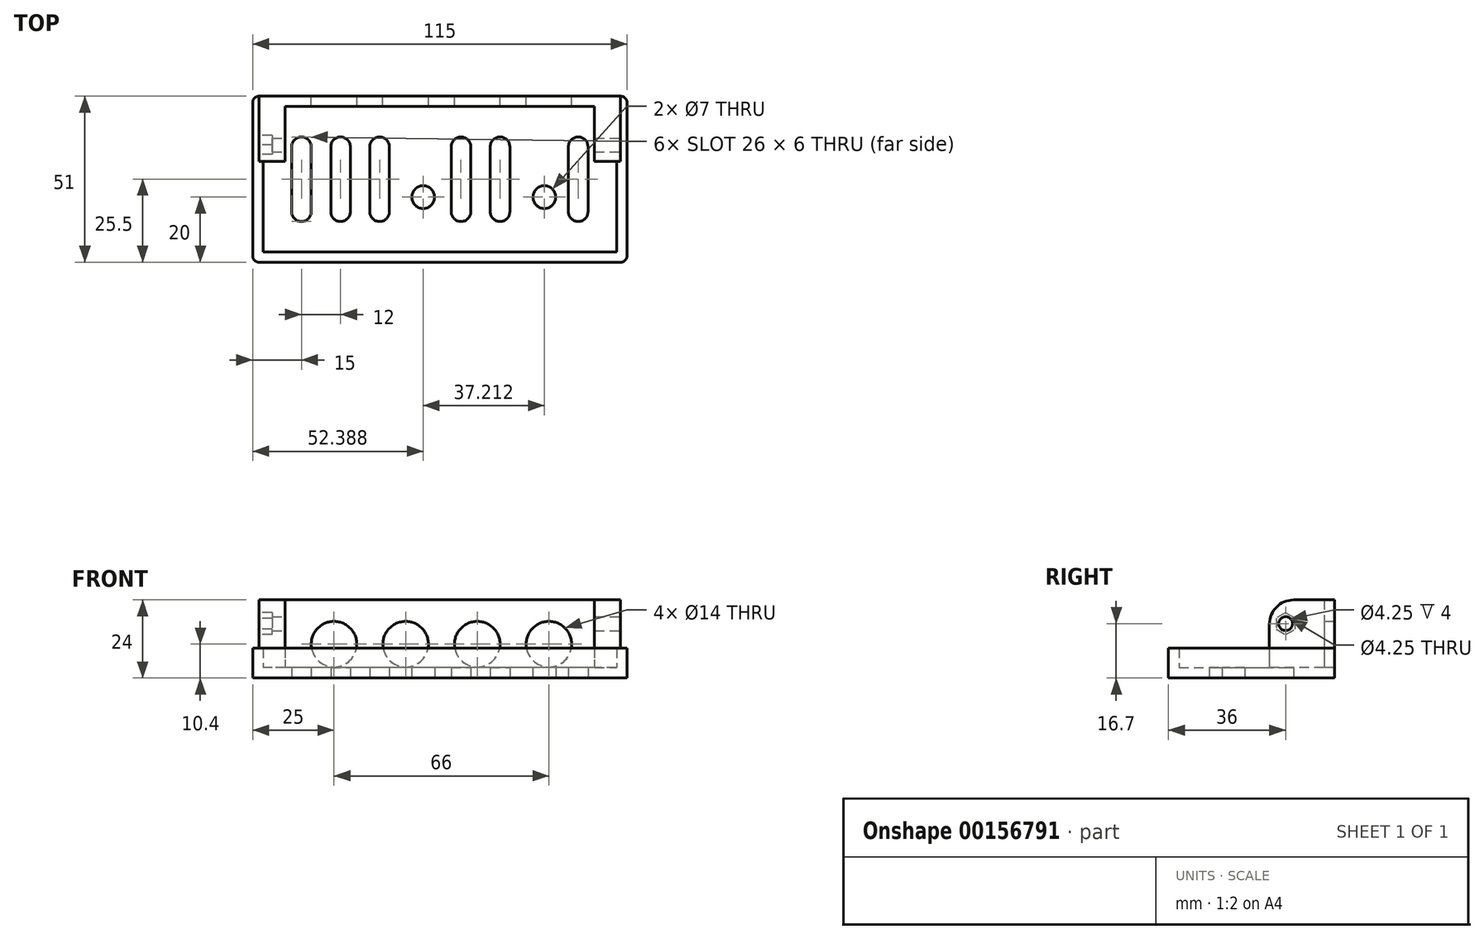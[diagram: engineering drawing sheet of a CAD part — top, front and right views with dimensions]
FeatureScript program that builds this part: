
annotation { "Feature Type Name" : "Feature", "Feature Type Description" : "" }
export const myFeature = defineFeature(function(context is Context, id is Id, definition is map)
    precondition{}
    {
        {
            var Q0;
            Q0=qCreatedBy(makeId("Top.planeOp"),FACE);
            var sketch = newSketch(context, id + "F0", { "sketchPlane" : qUnion([Q0])});
            skLineSegment(sketch, "E0.bottom", {"start": v(57.5, -25.5) * mm, "end": v(-57.5, -25.5) * mm});
            skLineSegment(sketch, "E0.top", {"start": v(57.5, 25.5) * mm, "end": v(-57.5, 25.5) * mm});
            skLineSegment(sketch, "E0.left", {"start": v(57.5, -25.5) * mm, "end": v(57.5, 25.5) * mm});
            skLineSegment(sketch, "E0.right", {"start": v(-57.5, -25.5) * mm, "end": v(-57.5, 25.5) * mm});
            skPoint(sketch, "E0.middle", {"position": v(0, 0) * mm});
            skLineSegment(sketch, "E1.bottom", {"start": v(-42.5, -13) * mm, "end": v(-42.5, -13) * mm});
            skLineSegment(sketch, "E1.top", {"start": v(-42.5, 13) * mm, "end": v(-42.5, 13) * mm});
            skLineSegment(sketch, "E1.left", {"start": v(-39.5, -10) * mm, "end": v(-39.5, 10) * mm});
            skLineSegment(sketch, "E1.right", {"start": v(-45.5, -10) * mm, "end": v(-45.5, 10) * mm});
            skPoint(sketch, "E1.middle", {"position": v(-42.5, 0) * mm});
            skLineSegment(sketch, "E2.bottom", {"start": v(-30.5, -13) * mm, "end": v(-30.5, -13) * mm});
            skLineSegment(sketch, "E2.top", {"start": v(-30.5, 13) * mm, "end": v(-30.5, 13) * mm});
            skLineSegment(sketch, "E2.left", {"start": v(-27.5, -10) * mm, "end": v(-27.5, 10) * mm});
            skLineSegment(sketch, "E2.right", {"start": v(-33.5, -10) * mm, "end": v(-33.5, 10) * mm});
            skPoint(sketch, "E2.middle", {"position": v(-30.5, 0) * mm});
            skLineSegment(sketch, "E3.bottom", {"start": v(-18.5, -13) * mm, "end": v(-18.5, -13) * mm});
            skLineSegment(sketch, "E3.top", {"start": v(-18.5, 13) * mm, "end": v(-18.5, 13) * mm});
            skLineSegment(sketch, "E3.left", {"start": v(-15.5, -10) * mm, "end": v(-15.5, 10) * mm});
            skLineSegment(sketch, "E3.right", {"start": v(-21.5, -10) * mm, "end": v(-21.5, 10) * mm});
            skPoint(sketch, "E3.middle", {"position": v(-18.5, 0) * mm});
            skLineSegment(sketch, "E4.bottom", {"start": v(6.5, -13) * mm, "end": v(6.5, -13) * mm});
            skLineSegment(sketch, "E4.top", {"start": v(6.5, 13) * mm, "end": v(6.5, 13) * mm});
            skLineSegment(sketch, "E4.left", {"start": v(9.5, -10) * mm, "end": v(9.5, 10) * mm});
            skLineSegment(sketch, "E4.right", {"start": v(3.5, -10) * mm, "end": v(3.5, 10) * mm});
            skPoint(sketch, "E4.middle", {"position": v(6.5, 0) * mm});
            skLineSegment(sketch, "E5.bottom", {"start": v(18.5, -13) * mm, "end": v(18.5, -13) * mm});
            skLineSegment(sketch, "E5.top", {"start": v(18.5, 13) * mm, "end": v(18.5, 13) * mm});
            skLineSegment(sketch, "E5.left", {"start": v(21.5, -10) * mm, "end": v(21.5, 10) * mm});
            skLineSegment(sketch, "E5.right", {"start": v(15.5, -10) * mm, "end": v(15.5, 10) * mm});
            skPoint(sketch, "E5.middle", {"position": v(18.5, 0) * mm});
            skLineSegment(sketch, "E6.bottom", {"start": v(42.5, -13) * mm, "end": v(42.5, -13) * mm});
            skLineSegment(sketch, "E6.top", {"start": v(42.5, 13) * mm, "end": v(42.5, 13) * mm});
            skLineSegment(sketch, "E6.left", {"start": v(45.5, -10) * mm, "end": v(45.5, 10) * mm});
            skLineSegment(sketch, "E6.right", {"start": v(39.5, -10) * mm, "end": v(39.5, 10) * mm});
            skPoint(sketch, "E6.middle", {"position": v(42.5, 0) * mm});
            skCircle(sketch, "E7", {"center": v(32.1, -5.5) * mm, "radius": 3.5 * mm});
            skCircle(sketch, "E8", {"center": v(-5.11, -5.5) * mm, "radius": 3.5 * mm});
            skPoint(sketch, "E9.visualSharp", {"position": v(-45.5, 13) * mm});
            skArc(sketch, "E9.filletArc", {"start": v(-42.5, 13) * mm, "mid": v(-44.62, 12.12) * mm, "end": v(-45.5, 10) * mm});
            skPoint(sketch, "E10.visualSharp", {"position": v(-39.5, 13) * mm});
            skArc(sketch, "E10.filletArc", {"start": v(-39.5, 10) * mm, "mid": v(-40.38, 12.12) * mm, "end": v(-42.5, 13) * mm});
            skPoint(sketch, "E11.visualSharp", {"position": v(-39.5, -13) * mm});
            skArc(sketch, "E11.filletArc", {"start": v(-42.5, -13) * mm, "mid": v(-40.38, -12.12) * mm, "end": v(-39.5, -10) * mm});
            skPoint(sketch, "E12.visualSharp", {"position": v(-45.5, -13) * mm});
            skArc(sketch, "E12.filletArc", {"start": v(-45.5, -10) * mm, "mid": v(-44.62, -12.12) * mm, "end": v(-42.5, -13) * mm});
            skPoint(sketch, "E13.visualSharp", {"position": v(-33.5, -13) * mm});
            skArc(sketch, "E13.filletArc", {"start": v(-33.5, -10) * mm, "mid": v(-32.62, -12.12) * mm, "end": v(-30.5, -13) * mm});
            skPoint(sketch, "E14.visualSharp", {"position": v(-27.5, -13) * mm});
            skArc(sketch, "E14.filletArc", {"start": v(-30.5, -13) * mm, "mid": v(-28.38, -12.12) * mm, "end": v(-27.5, -10) * mm});
            skPoint(sketch, "E15.visualSharp", {"position": v(-27.5, 13) * mm});
            skArc(sketch, "E15.filletArc", {"start": v(-27.5, 10) * mm, "mid": v(-28.38, 12.12) * mm, "end": v(-30.5, 13) * mm});
            skPoint(sketch, "E16.visualSharp", {"position": v(-33.5, 13) * mm});
            skArc(sketch, "E16.filletArc", {"start": v(-30.5, 13) * mm, "mid": v(-32.62, 12.12) * mm, "end": v(-33.5, 10) * mm});
            skPoint(sketch, "E17.visualSharp", {"position": v(-21.5, 13) * mm});
            skArc(sketch, "E17.filletArc", {"start": v(-18.5, 13) * mm, "mid": v(-20.62, 12.12) * mm, "end": v(-21.5, 10) * mm});
            skPoint(sketch, "E18.visualSharp", {"position": v(-15.5, 13) * mm});
            skArc(sketch, "E18.filletArc", {"start": v(-15.5, 10) * mm, "mid": v(-16.38, 12.12) * mm, "end": v(-18.5, 13) * mm});
            skPoint(sketch, "E19.visualSharp", {"position": v(-15.5, -13) * mm});
            skArc(sketch, "E19.filletArc", {"start": v(-18.5, -13) * mm, "mid": v(-16.38, -12.12) * mm, "end": v(-15.5, -10) * mm});
            skPoint(sketch, "E20.visualSharp", {"position": v(-21.5, -13) * mm});
            skArc(sketch, "E20.filletArc", {"start": v(-21.5, -10) * mm, "mid": v(-20.62, -12.12) * mm, "end": v(-18.5, -13) * mm});
            skPoint(sketch, "E21.visualSharp", {"position": v(3.5, -13) * mm});
            skArc(sketch, "E21.filletArc", {"start": v(3.5, -10) * mm, "mid": v(4.38, -12.12) * mm, "end": v(6.5, -13) * mm});
            skPoint(sketch, "E22.visualSharp", {"position": v(9.5, -13) * mm});
            skArc(sketch, "E22.filletArc", {"start": v(6.5, -13) * mm, "mid": v(8.62, -12.12) * mm, "end": v(9.5, -10) * mm});
            skPoint(sketch, "E23.visualSharp", {"position": v(9.5, 13) * mm});
            skArc(sketch, "E23.filletArc", {"start": v(9.5, 10) * mm, "mid": v(8.62, 12.12) * mm, "end": v(6.5, 13) * mm});
            skPoint(sketch, "E24.visualSharp", {"position": v(3.5, 13) * mm});
            skArc(sketch, "E24.filletArc", {"start": v(6.5, 13) * mm, "mid": v(4.38, 12.12) * mm, "end": v(3.5, 10) * mm});
            skPoint(sketch, "E25.visualSharp", {"position": v(15.5, -13) * mm});
            skArc(sketch, "E25.filletArc", {"start": v(15.5, -10) * mm, "mid": v(16.38, -12.12) * mm, "end": v(18.5, -13) * mm});
            skPoint(sketch, "E26.visualSharp", {"position": v(21.5, -13) * mm});
            skArc(sketch, "E26.filletArc", {"start": v(18.5, -13) * mm, "mid": v(20.62, -12.12) * mm, "end": v(21.5, -10) * mm});
            skPoint(sketch, "E27.visualSharp", {"position": v(21.5, 13) * mm});
            skArc(sketch, "E27.filletArc", {"start": v(21.5, 10) * mm, "mid": v(20.62, 12.12) * mm, "end": v(18.5, 13) * mm});
            skPoint(sketch, "E28.visualSharp", {"position": v(15.5, 13) * mm});
            skArc(sketch, "E28.filletArc", {"start": v(18.5, 13) * mm, "mid": v(16.38, 12.12) * mm, "end": v(15.5, 10) * mm});
            skPoint(sketch, "E29.visualSharp", {"position": v(39.5, -13) * mm});
            skArc(sketch, "E29.filletArc", {"start": v(39.5, -10) * mm, "mid": v(40.38, -12.12) * mm, "end": v(42.5, -13) * mm});
            skPoint(sketch, "E30.visualSharp", {"position": v(45.5, 13) * mm});
            skArc(sketch, "E30.filletArc", {"start": v(45.5, 10) * mm, "mid": v(44.62, 12.12) * mm, "end": v(42.5, 13) * mm});
            skPoint(sketch, "E31.visualSharp", {"position": v(39.5, 13) * mm});
            skArc(sketch, "E31.filletArc", {"start": v(42.5, 13) * mm, "mid": v(40.38, 12.12) * mm, "end": v(39.5, 10) * mm});
            skPoint(sketch, "E32.visualSharp", {"position": v(45.5, -13) * mm});
            skArc(sketch, "E32.filletArc", {"start": v(42.5, -13) * mm, "mid": v(44.62, -12.12) * mm, "end": v(45.5, -10) * mm});
            skSolve(sketch);
        }
        {
            var Q0;
            Q0 = qSketchRegion(id + "F0", true);
            extrude(context, id + "F1", {"entities" : qUnion([Q0]), "depth" : 3.2 * mm});
        }
        {
            var Q0;
            Q0=makeQuery(id+"F1.opExtrude","CAP_FACE",FACE,{"disambiguationData":[OSD([sQuery(id+"F0.wireOp",EDGE,"E0.bottom"),sQuery(id+"F0.wireOp",EDGE,"E0.top"),sQuery(id+"F0.wireOp",EDGE,"E0.left"),sQuery(id+"F0.wireOp",EDGE,"E0.right"),sQuery(id+"F0.wireOp",EDGE,"E1.bottom"),sQuery(id+"F0.wireOp",EDGE,"E1.top"),sQuery(id+"F0.wireOp",EDGE,"E1.left"),sQuery(id+"F0.wireOp",EDGE,"E1.right"),sQuery(id+"F0.wireOp",EDGE,"E2.bottom"),sQuery(id+"F0.wireOp",EDGE,"E2.top"),sQuery(id+"F0.wireOp",EDGE,"E2.left"),sQuery(id+"F0.wireOp",EDGE,"E2.right"),sQuery(id+"F0.wireOp",EDGE,"E3.bottom"),sQuery(id+"F0.wireOp",EDGE,"E3.top"),sQuery(id+"F0.wireOp",EDGE,"E3.left"),sQuery(id+"F0.wireOp",EDGE,"E3.right"),sQuery(id+"F0.wireOp",EDGE,"E4.bottom"),sQuery(id+"F0.wireOp",EDGE,"E4.top"),sQuery(id+"F0.wireOp",EDGE,"E4.left"),sQuery(id+"F0.wireOp",EDGE,"E4.right"),sQuery(id+"F0.wireOp",EDGE,"E5.bottom"),sQuery(id+"F0.wireOp",EDGE,"E5.top"),sQuery(id+"F0.wireOp",EDGE,"E5.left"),sQuery(id+"F0.wireOp",EDGE,"E5.right"),sQuery(id+"F0.wireOp",EDGE,"E6.bottom"),sQuery(id+"F0.wireOp",EDGE,"E6.top"),sQuery(id+"F0.wireOp",EDGE,"E6.left"),sQuery(id+"F0.wireOp",EDGE,"E6.right"),sQuery(id+"F0.wireOp",EDGE,"E7"),sQuery(id+"F0.wireOp",EDGE,"E8")])],"isStart":true});
            var sketch = newSketch(context, id + "F2", { "sketchPlane" : qUnion([Q0])});
            skLineSegment(sketch, "E33", {"start": v(-55.5, -5.5) * mm, "end": v(-55.5, -25.5) * mm});
            skLineSegment(sketch, "E34", {"start": v(-55.5, -25.5) * mm, "end": v(55.5, -25.5) * mm});
            skLineSegment(sketch, "E35", {"start": v(55.5, -25.5) * mm, "end": v(55.5, -5.5) * mm});
            skLineSegment(sketch, "E36", {"start": v(55.5, -5.5) * mm, "end": v(47.5, -5.5) * mm});
            skLineSegment(sketch, "E37", {"start": v(47.5, -5.5) * mm, "end": v(47.5, -22.3) * mm});
            skLineSegment(sketch, "E38", {"start": v(-55.5, -5.5) * mm, "end": v(-47.5, -5.5) * mm});
            skLineSegment(sketch, "E39", {"start": v(-47.5, -5.5) * mm, "end": v(-47.5, -22.3) * mm});
            skLineSegment(sketch, "E40", {"start": v(-47.5, -22.3) * mm, "end": v(47.5, -22.3) * mm});
            skSolve(sketch);
        }
        {
            var Q0;
            Q0 = qSketchRegion(id + "F2", true);
            extrude(context, id + "F3", {"entities" : qUnion([Q0]), "operationType" : NewBodyOperationType.ADD, "oppositeDirection" : true, "depth" : 24 * mm});
        }
        {
            var Q0;
            Q0=makeQuery(id+"F1.opExtrude","CAP_FACE",FACE,{"disambiguationData":[OSD([sQuery(id+"F0.wireOp",EDGE,"E0.bottom"),sQuery(id+"F0.wireOp",EDGE,"E0.top"),sQuery(id+"F0.wireOp",EDGE,"E0.left"),sQuery(id+"F0.wireOp",EDGE,"E0.right"),sQuery(id+"F0.wireOp",EDGE,"E1.left"),sQuery(id+"F0.wireOp",EDGE,"E1.right"),sQuery(id+"F0.wireOp",EDGE,"E2.left"),sQuery(id+"F0.wireOp",EDGE,"E2.right"),sQuery(id+"F0.wireOp",EDGE,"E3.left"),sQuery(id+"F0.wireOp",EDGE,"E3.right"),sQuery(id+"F0.wireOp",EDGE,"E4.left"),sQuery(id+"F0.wireOp",EDGE,"E4.right"),sQuery(id+"F0.wireOp",EDGE,"E5.left"),sQuery(id+"F0.wireOp",EDGE,"E5.right"),sQuery(id+"F0.wireOp",EDGE,"E6.left"),sQuery(id+"F0.wireOp",EDGE,"E6.right"),sQuery(id+"F0.wireOp",EDGE,"E7"),sQuery(id+"F0.wireOp",EDGE,"E8"),sQuery(id+"F0.wireOp",EDGE,"E9.filletArc"),sQuery(id+"F0.wireOp",EDGE,"E10.filletArc"),sQuery(id+"F0.wireOp",EDGE,"E11.filletArc"),sQuery(id+"F0.wireOp",EDGE,"E12.filletArc"),sQuery(id+"F0.wireOp",EDGE,"E13.filletArc"),sQuery(id+"F0.wireOp",EDGE,"E14.filletArc"),sQuery(id+"F0.wireOp",EDGE,"E15.filletArc"),sQuery(id+"F0.wireOp",EDGE,"E16.filletArc"),sQuery(id+"F0.wireOp",EDGE,"E17.filletArc"),sQuery(id+"F0.wireOp",EDGE,"E18.filletArc"),sQuery(id+"F0.wireOp",EDGE,"E19.filletArc"),sQuery(id+"F0.wireOp",EDGE,"E20.filletArc"),sQuery(id+"F0.wireOp",EDGE,"E21.filletArc"),sQuery(id+"F0.wireOp",EDGE,"E22.filletArc"),sQuery(id+"F0.wireOp",EDGE,"E23.filletArc"),sQuery(id+"F0.wireOp",EDGE,"E24.filletArc"),sQuery(id+"F0.wireOp",EDGE,"E25.filletArc"),sQuery(id+"F0.wireOp",EDGE,"E26.filletArc"),sQuery(id+"F0.wireOp",EDGE,"E27.filletArc"),sQuery(id+"F0.wireOp",EDGE,"E28.filletArc"),sQuery(id+"F0.wireOp",EDGE,"E29.filletArc"),sQuery(id+"F0.wireOp",EDGE,"E30.filletArc"),sQuery(id+"F0.wireOp",EDGE,"E31.filletArc"),sQuery(id+"F0.wireOp",EDGE,"E32.filletArc")])],"isStart":false});
            var sketch = newSketch(context, id + "F4", { "sketchPlane" : qUnion([Q0])});
            skLineSegment(sketch, "E41", {"start": v(-55.5, 25.5) * mm, "end": v(-57.5, 25.5) * mm});
            skLineSegment(sketch, "E42", {"start": v(-57.5, 25.5) * mm, "end": v(-57.5, -25.5) * mm});
            skLineSegment(sketch, "E43", {"start": v(-57.5, -25.5) * mm, "end": v(57.5, -25.5) * mm});
            skLineSegment(sketch, "E44", {"start": v(57.5, -25.5) * mm, "end": v(57.5, 25.5) * mm});
            skLineSegment(sketch, "E45", {"start": v(57.5, 25.5) * mm, "end": v(55.5, 25.5) * mm});
            skLineSegment(sketch, "E46", {"start": v(55.5, 25.5) * mm, "end": v(55.5, 5.5) * mm});
            skLineSegment(sketch, "E47", {"start": v(55.5, 5.5) * mm, "end": v(54.3, 5.5) * mm});
            skLineSegment(sketch, "E48", {"start": v(54.3, 5.5) * mm, "end": v(54.3, -22.3) * mm});
            skLineSegment(sketch, "E49", {"start": v(54.3, -22.3) * mm, "end": v(-54.3, -22.3) * mm});
            skLineSegment(sketch, "E50", {"start": v(-54.3, -22.3) * mm, "end": v(-54.3, 5.5) * mm});
            skLineSegment(sketch, "E51", {"start": v(-54.3, 5.5) * mm, "end": v(-55.5, 5.5) * mm});
            skLineSegment(sketch, "E52", {"start": v(-55.5, 5.5) * mm, "end": v(-55.5, 25.5) * mm});
            skLineSegment(sketch, "E53", {"start": v(54.3, 5.5) * mm, "end": v(55.5, 5.5) * mm});
            skSolve(sketch);
        }
        {
            var Q0;
            Q0 = qSketchRegion(id + "F4", true);
            extrude(context, id + "F5", {"entities" : qUnion([Q0]), "operationType" : NewBodyOperationType.ADD, "depth" : 6 * mm});
        }
        {
            var Q0;
            Q0=makeQuery(id+"F3.opExtrude","SWEPT_FACE",FACE,{"disambiguationData":[OSD([sQuery(id+"F2.wireOp",EDGE,"E35")])]});
            var sketch = newSketch(context, id + "F6", { "sketchPlane" : qUnion([Q0])});
            skCircle(sketch, "E54", {"center": v(10.5, 16.7) * mm, "radius": 2.12 * mm});
            skSolve(sketch);
        }
        {
            var Q0;
            Q0 = qSketchRegion(id + "F6", true);
            extrude(context, id + "F7", {"entities" : qUnion([Q0]), "operationType" : NewBodyOperationType.REMOVE, "endBound" : BoundingType.THROUGH_ALL, "oppositeDirection" : true, "depth" : 25 * mm});
        }
        {
            var Q0;
            Q0=makeQuery(id+"F3.opExtrude","CAP_EDGE",EDGE,{"disambiguationData":[OSD([sQuery(id+"F2.wireOp",EDGE,"E36")])],"isStart":false});
            var Q1;
            Q1=makeQuery(id+"F3.opExtrude","CAP_EDGE",EDGE,{"disambiguationData":[OSD([sQuery(id+"F2.wireOp",EDGE,"E38")])],"isStart":false});
            fillet(context, id + "F8", {"entities" : qUnion([Q0, Q1]), "radius" : 7.5 * mm, "tangentPropagation" : true, "allowEdgeOverflow" : false});
        }
        {
            var Q0;
            Q0=makeQuery(id+"F5.boolean.opBoolean","MERGE",EDGE,{"derivedFrom":[makeQuery(id+"F1.opExtrude","SWEPT_EDGE",EDGE,{"disambiguationData":[OSD([sQuery(id+"F0.wireOp",EDGE,"E0.bottom"),sQuery(id+"F0.wireOp",EDGE,"E0.right")])]}),makeQuery(id+"F5.opExtrude","SWEPT_EDGE",EDGE,{"disambiguationData":[OSD([sQuery(id+"F4.wireOp",EDGE,"E42"),sQuery(id+"F4.wireOp",EDGE,"E43")])]})]});
            var Q1;
            Q1=makeQuery(id+"F5.boolean.opBoolean","MERGE",EDGE,{"derivedFrom":[makeQuery(id+"F1.opExtrude","SWEPT_EDGE",EDGE,{"disambiguationData":[OSD([sQuery(id+"F0.wireOp",EDGE,"E0.bottom"),sQuery(id+"F0.wireOp",EDGE,"E0.left")])]}),makeQuery(id+"F5.opExtrude","SWEPT_EDGE",EDGE,{"disambiguationData":[OSD([sQuery(id+"F4.wireOp",EDGE,"E43"),sQuery(id+"F4.wireOp",EDGE,"E44")])]})]});
            var Q2;
            Q2=makeQuery(id+"F5.boolean.opBoolean","MERGE",EDGE,{"derivedFrom":[makeQuery(id+"F1.opExtrude","SWEPT_EDGE",EDGE,{"disambiguationData":[OSD([sQuery(id+"F0.wireOp",EDGE,"E0.top"),sQuery(id+"F0.wireOp",EDGE,"E0.left")])]}),makeQuery(id+"F5.opExtrude","SWEPT_EDGE",EDGE,{"disambiguationData":[OSD([sQuery(id+"F4.wireOp",EDGE,"E44"),sQuery(id+"F4.wireOp",EDGE,"E45")])]})]});
            var Q3;
            Q3=makeQuery(id+"F5.boolean.opBoolean","MERGE",EDGE,{"derivedFrom":[makeQuery(id+"F1.opExtrude","SWEPT_EDGE",EDGE,{"disambiguationData":[OSD([sQuery(id+"F0.wireOp",EDGE,"E0.top"),sQuery(id+"F0.wireOp",EDGE,"E0.right")])]}),makeQuery(id+"F5.opExtrude","SWEPT_EDGE",EDGE,{"disambiguationData":[OSD([sQuery(id+"F4.wireOp",EDGE,"E41"),sQuery(id+"F4.wireOp",EDGE,"E42")])]})]});
            fillet(context, id + "F9", {"entities" : qUnion([Q0, Q1, Q2, Q3]), "radius" : 2 * mm, "tangentPropagation" : true, "allowEdgeOverflow" : false});
        }
        {
            var Q0;
            Q0=makeQuery(id+"F5.boolean.opBoolean","MERGE",FACE,{"derivedFrom":[makeQuery(id+"F3.boolean.opBoolean","MERGE",FACE,{"derivedFrom":[makeQuery(id+"F1.opExtrude","SWEPT_FACE",FACE,{"disambiguationData":[OSD([sQuery(id+"F0.wireOp",EDGE,"E0.top")])]}),makeQuery(id+"F3.opExtrude","SWEPT_FACE",FACE,{"disambiguationData":[OSD([sQuery(id+"F2.wireOp",EDGE,"E34")])]})]}),makeQuery(id+"F5.opExtrude","SWEPT_FACE",FACE,{"disambiguationData":[OSD([sQuery(id+"F4.wireOp",EDGE,"E41")])]}),makeQuery(id+"F5.opExtrude","SWEPT_FACE",FACE,{"disambiguationData":[OSD([sQuery(id+"F4.wireOp",EDGE,"E45")])]})]});
            var sketch = newSketch(context, id + "F10", { "sketchPlane" : qUnion([Q0])});
            skCircle(sketch, "E55", {"center": v(-33.5, 10.4) * mm, "radius": 7 * mm});
            skCircle(sketch, "E56.1.0.0", {"center": v(-11.5, 10.4) * mm, "radius": 7 * mm});
            skCircle(sketch, "E56.2.0.0", {"center": v(10.5, 10.4) * mm, "radius": 7 * mm});
            skCircle(sketch, "E56.3.0.0", {"center": v(32.5, 10.4) * mm, "radius": 7 * mm});
            skLineSegment(sketch, "E56.direction1", {"start": v(-33.5, 10.4) * mm, "end": v(-11.5, 10.4) * mm, "construction": true});
            skSolve(sketch);
        }
        {
            var Q0;
            Q0 = qSketchRegion(id + "F10", true);
            extrude(context, id + "F11", {"entities" : qUnion([Q0]), "operationType" : NewBodyOperationType.REMOVE, "oppositeDirection" : true, "depth" : 5 * mm});
        }
        {
            var Q0;
            Q0=makeQuery(id+"F3.opExtrude","SWEPT_FACE",FACE,{"disambiguationData":[OSD([sQuery(id+"F2.wireOp",EDGE,"E33")])]});
            var sketch = newSketch(context, id + "F12", { "sketchPlane" : qUnion([Q0])});
            skCircle(sketch, "E57.cCircle", {"center": v(-10.5, 16.7) * mm, "radius": 2.93 * mm, "construction": true});
            skLineSegment(sketch, "E57.0", {"start": v(-7.57, 18.39) * mm, "end": v(-7.57, 15.01) * mm});
            skLineSegment(sketch, "E57.1", {"start": v(-7.57, 15.01) * mm, "end": v(-10.5, 13.32) * mm});
            skLineSegment(sketch, "E57.2", {"start": v(-10.5, 13.32) * mm, "end": v(-13.42, 15.01) * mm});
            skLineSegment(sketch, "E57.3", {"start": v(-13.42, 15.01) * mm, "end": v(-13.42, 18.39) * mm});
            skLineSegment(sketch, "E57.4", {"start": v(-13.42, 18.39) * mm, "end": v(-10.5, 20.08) * mm});
            skLineSegment(sketch, "E57.5", {"start": v(-10.5, 20.08) * mm, "end": v(-7.57, 18.39) * mm});
            skPoint(sketch, "E57.0.midPoint", {"position": v(-7.57, 16.7) * mm});
            skSolve(sketch);
        }
        {
            var Q0;
            Q0 = qSketchRegion(id + "F12", true);
            extrude(context, id + "F13", {"entities" : qUnion([Q0]), "operationType" : NewBodyOperationType.REMOVE, "oppositeDirection" : true, "depth" : 4 * mm});
        }
    });
